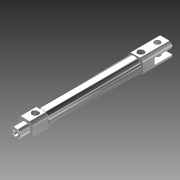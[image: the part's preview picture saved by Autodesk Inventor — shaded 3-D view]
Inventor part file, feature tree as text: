
AUTODESK INVENTOR PART (.ipt)
format: ipt  version: 2014 SP1 (Build 180222100, 222)  size: 158,720 bytes
history: native  units: in
note: dims shown in document units (in); Inventor stores cm internally (conversion verified against a paired STEP export)
features: thread x2, other x1, imported_body x1, extrude x1, sketch x1, projected_geometry x1
ambient origin geometry x8: Origin, YZ Plane, XZ Plane, XY Plane, X Axis, Y Axis, Z Axis, Center Point
bodies: Body1 (feature_tree)
feature tree (7):
  parser-record x1  (decoder bookkeeping rows leaked as tree rows — omitted from the tree; the rows remain in map.json)
  imported_body  "Base1"
  thread  "Thread1"  [1 undecoded]
  thread  "Thread2"  [1 undecoded]
  extrude  "Extrusion1"  [1 undecoded]
  sketch  "Sketch1"  dims[d4=0.3937in d5=0.0in]
  projected_geometry  "Projected Loop1"
note: 3 required parameter values undecoded (feature->parameter linkage not recoverable at this tier; creation-order binding heuristic only, values carry confidence <= 0.55)
